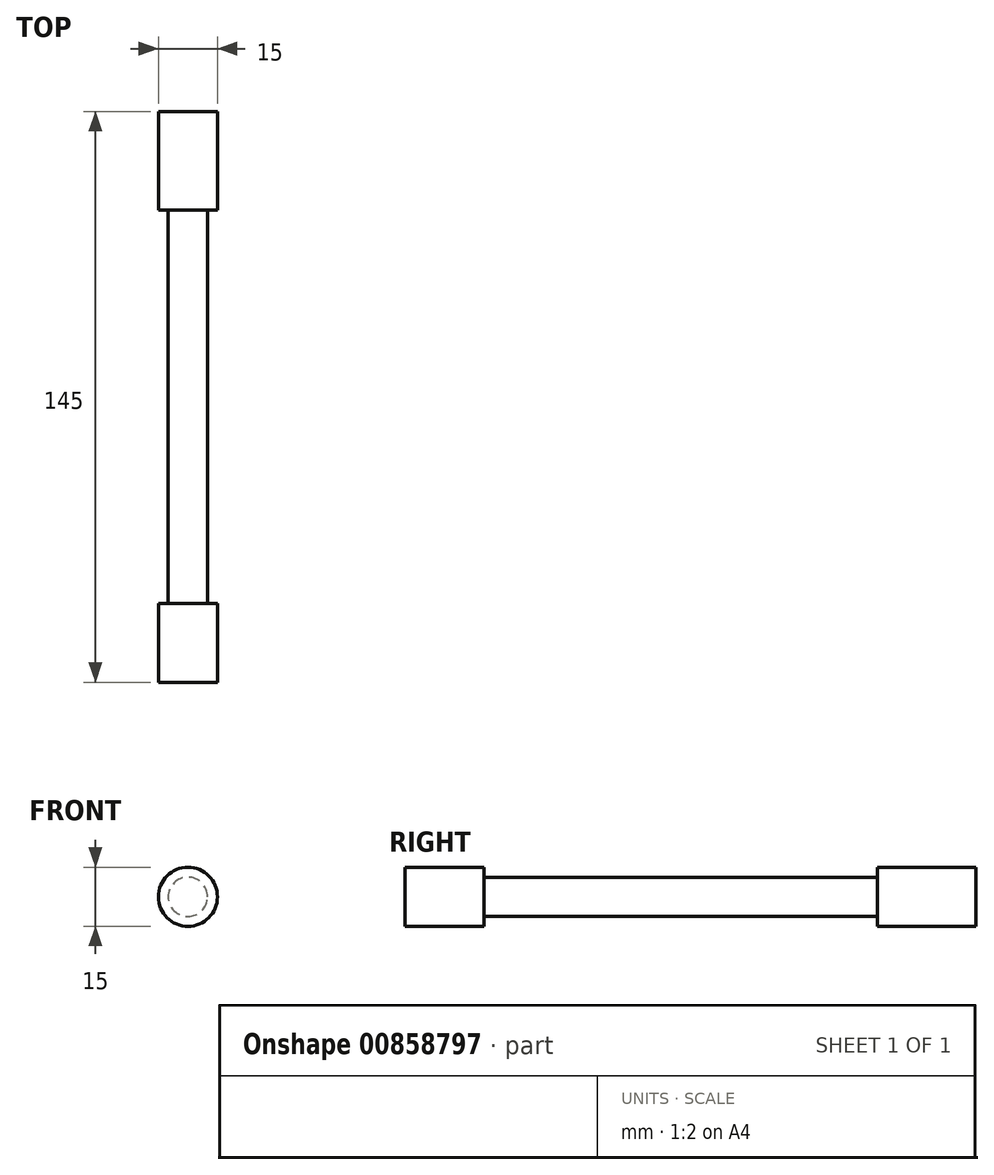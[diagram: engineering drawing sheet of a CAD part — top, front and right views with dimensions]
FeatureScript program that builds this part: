
annotation { "Feature Type Name" : "Feature", "Feature Type Description" : "" }
export const myFeature = defineFeature(function(context is Context, id is Id, definition is map)
    precondition{}
    {
        {
            var Q0;
            Q0=qCreatedBy(makeId("Front.planeOp"),FACE);
            var sketch = newSketch(context, id + "F0", { "sketchPlane" : qUnion([Q0])});
            skCircle(sketch, "E0", {"center": v(0, 0) * mm, "radius": 5 * mm});
            skSolve(sketch);
        }
        {
            var Q0;
            Q0=makeQuery(id+"F0.imprint","IMPRINT",FACE,{"disambiguationData":[TD([[makeQuery(id+"F0.imprint","IMPRINT",EDGE,{"derivedFrom":sQuery(id+"F0.wireOp",EDGE,"E0")}),1.0]])]});
            extrude(context, id + "F1", {"entities" : qUnion([Q0]), "depth" : 100 * mm, "offsetDistance" : 25 * mm});
        }
        {
            var Q0;
            Q0=makeQuery(id+"F1.opExtrude","CAP_FACE",FACE,{"disambiguationData":[OSD([sQuery(id+"F0.wireOp",EDGE,"E0")])],"isStart":false});
            var sketch = newSketch(context, id + "F2", { "sketchPlane" : qUnion([Q0])});
            skCircle(sketch, "E1", {"center": v(0, 0) * mm, "radius": 7.5 * mm});
            skSolve(sketch);
        }
        {
            var Q0;
            Q0=makeQuery(id+"F2.imprint","IMPRINT",FACE,{"disambiguationData":[TD([[makeQuery(id+"F2.imprint","IMPRINT",EDGE,{"derivedFrom":makeQuery(id+"F1.opExtrude","CAP_EDGE",EDGE,{"disambiguationData":[OSD([sQuery(id+"F0.wireOp",EDGE,"E0")])],"isStart":false})}),1.0]])]});
            var Q1;
            Q1=makeQuery(id+"F2.imprint","IMPRINT",FACE,{"disambiguationData":[TD([[makeQuery(id+"F2.imprint","IMPRINT",EDGE,{"derivedFrom":sQuery(id+"F2.wireOp",EDGE,"E1")}),1.0]])]});
            extrude(context, id + "F3", {"entities" : qUnion([Q0, Q1]), "operationType" : NewBodyOperationType.ADD, "depth" : 20 * mm, "offsetDistance" : 25 * mm});
        }
        {
            var Q0;
            Q0=makeQuery(id+"F1.opExtrude","CAP_FACE",FACE,{"disambiguationData":[OSD([sQuery(id+"F0.wireOp",EDGE,"E0")])],"isStart":true});
            var sketch = newSketch(context, id + "F4", { "sketchPlane" : qUnion([Q0])});
            skCircle(sketch, "E2", {"center": v(0, 0) * mm, "radius": 7.5 * mm});
            skSolve(sketch);
        }
        {
            var Q0;
            Q0=makeQuery(id+"F4.imprint","IMPRINT",FACE,{"disambiguationData":[TD([[makeQuery(id+"F4.imprint","IMPRINT",EDGE,{"derivedFrom":sQuery(id+"F4.wireOp",EDGE,"E2")}),1.0]])]});
            var Q1;
            Q1=makeQuery(id+"F4.imprint","IMPRINT",FACE,{"disambiguationData":[TD([[makeQuery(id+"F4.imprint","IMPRINT",EDGE,{"derivedFrom":makeQuery(id+"F1.opExtrude","CAP_EDGE",EDGE,{"disambiguationData":[OSD([sQuery(id+"F0.wireOp",EDGE,"E0")])],"isStart":true})}),-1.0]])]});
            extrude(context, id + "F5", {"entities" : qUnion([Q0, Q1]), "operationType" : NewBodyOperationType.ADD, "depth" : 25 * mm, "offsetDistance" : 25 * mm});
        }
    });
